# Revit family: Diverter_Trim-3_Way-Grohe-Lineare-29215_Series
name_source: partatom
category: Plumbing Fixtures
units: mm (PartAtom-declared; Revit-internal decimal feet)

## family parameters
Cut with Voids When Loaded = No
Host = Face
OmniClass Number = 23.45.05.14.17
OmniClass Title = Showers
Part Type = Normal
Room Calculation Point = No
Round Connector Dimension = Use Diameter
Shared = Yes

## types (2) — shared parameters
ADA Compliant = Yes
Assembly Code = D2010710
CW Connection = No
CWFU = 3
Compliance Certifications = • ADA• CSA B125.1• ASME A112.18.1
Default Elevation = 44"
Description = Lineare 3-Way Diverter
HW Connection = No
HWFU = 3
Height = 4 13/16"
Installation Type = Wall Mounted
Length = 2 5/8"
Manufacturer = Grohe
Product Documentation Link = https://americanstandard.box.com
Product Page URL = https://www.grohe.us
Revised Date = 06/06/2023
Tempered Connection Diameter = 1/2"
Tempered Connection Radius = 1/4"
Tempered Water Connection = Yes
URL = https://www.grohe.us
Vent Connection = No
Warranty Information = Limited lifetime warranty
Waste Connection = No
Width = 3 1/8"
zero-valued in all types: WFU

## per-type parameters (varying)
| type | Finish | Material |
| 29215001 | Metal-Grohe-001-StarLight Chrome | Metal-Grohe-001-StarLight Chrome |
| 29215EN1 | Metal-Grohe-EN1-Brushed Nickel | Metal-Grohe-EN1-Brushed Nickel |

note: column(s) folded — value = type name in every type: Model

## geometry (parser evidence)
native form markers: Sweep x5
no freeform markers — native parametric forms only
